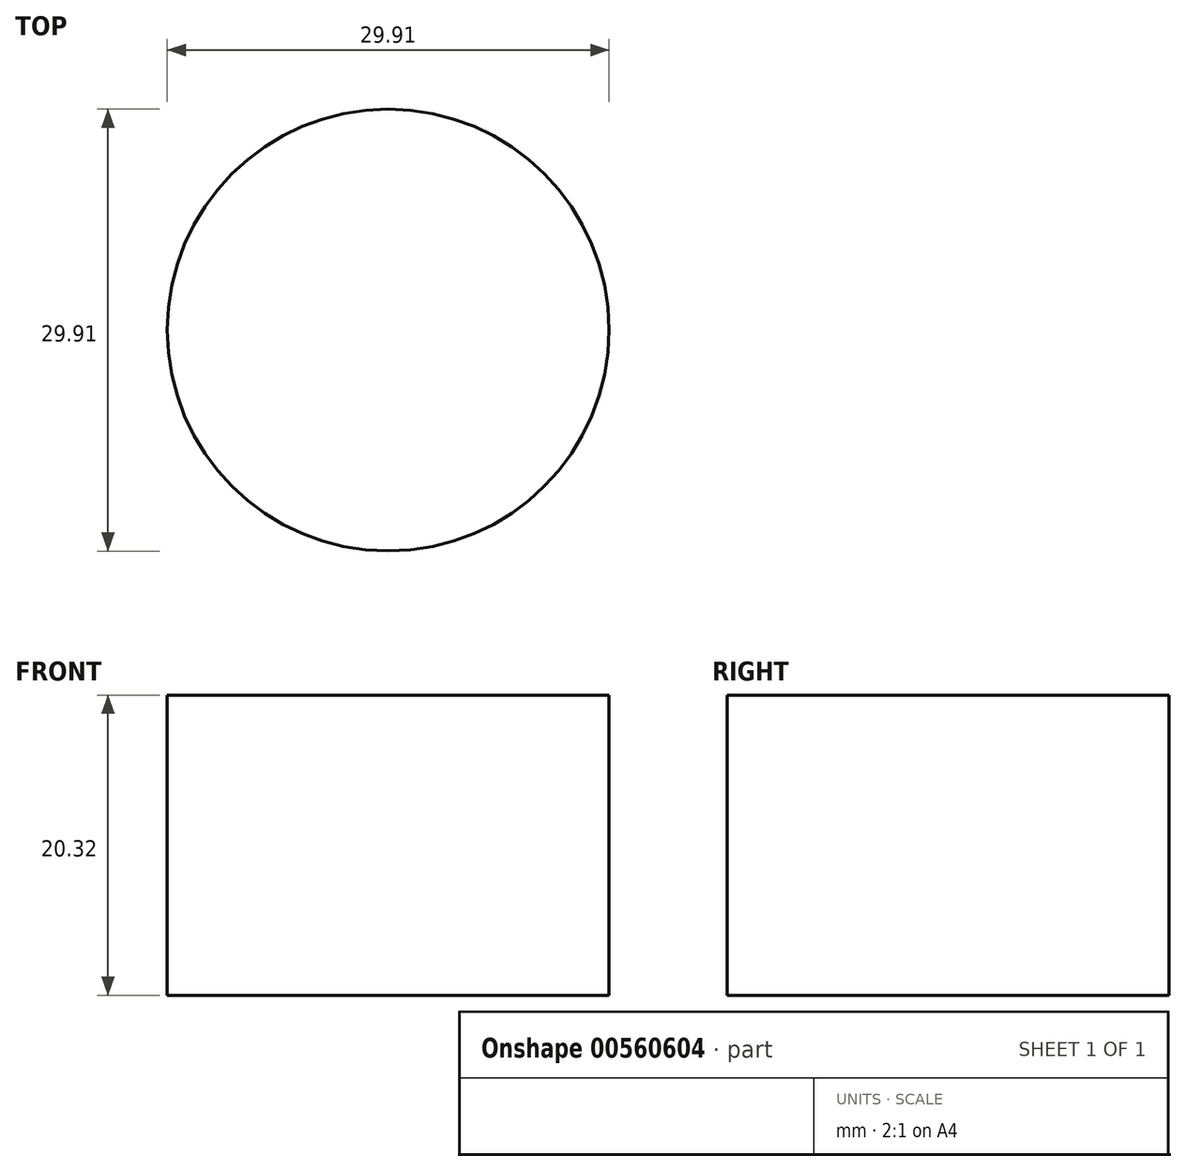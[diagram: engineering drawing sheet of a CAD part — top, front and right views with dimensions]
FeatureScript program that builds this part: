
annotation { "Feature Type Name" : "Feature", "Feature Type Description" : "" }
export const myFeature = defineFeature(function(context is Context, id is Id, definition is map)
    precondition{}
    {
        {
            var Q0;
            Q0=qCreatedBy(makeId("Top.planeOp"),FACE);
            var sketch = newSketch(context, id + "F0", { "sketchPlane" : qUnion([Q0])});
            skCircle(sketch, "E0", {"center": v(6.78, 5.65) * mm, "radius": 14.95 * mm});
            skSolve(sketch);
        }
        {
            var Q0;
            Q0=makeQuery(id+"F0.imprint","IMPRINT",FACE,{"disambiguationData":[TD([[makeQuery(id+"F0.imprint","IMPRINT",EDGE,{"derivedFrom":sQuery(id+"F0.wireOp",EDGE,"E0")}),1.0]])]});
            extrude(context, id + "F1", {"entities" : qUnion([Q0]), "oppositeDirection" : true, "depth" : 20.32 * mm, "offsetDistance" : 25.4 * mm});
        }
        {
            var Q0;
            Q0=qCreatedBy(makeId("Top.planeOp"),FACE);
            var sketch = newSketch(context, id + "F2", { "sketchPlane" : qUnion([Q0])});
            skLineSegment(sketch, "E1", {"start": v(-4.82, -3.77) * mm, "end": v(-4.72, -3.77) * mm});
            skLineSegment(sketch, "E2", {"start": v(-4.72, -3.77) * mm, "end": v(-4.72, -3.91) * mm});
            skSolve(sketch);
        }
        {
            var Q0;
            Q0=sQuery(id+"F2.wireOp",EDGE,"E2");
            var Q1;
            Q1=sQuery(id+"F2.wireOp",EDGE,"E1");
            extrude(context, id + "F3", {"bodyType" : ToolBodyType.SURFACE, "surfaceEntities" : qUnion([Q0, Q1]), "oppositeDirection" : true, "depth" : 25.65 * mm, "offsetDistance" : 25.4 * mm});
        }
    });
